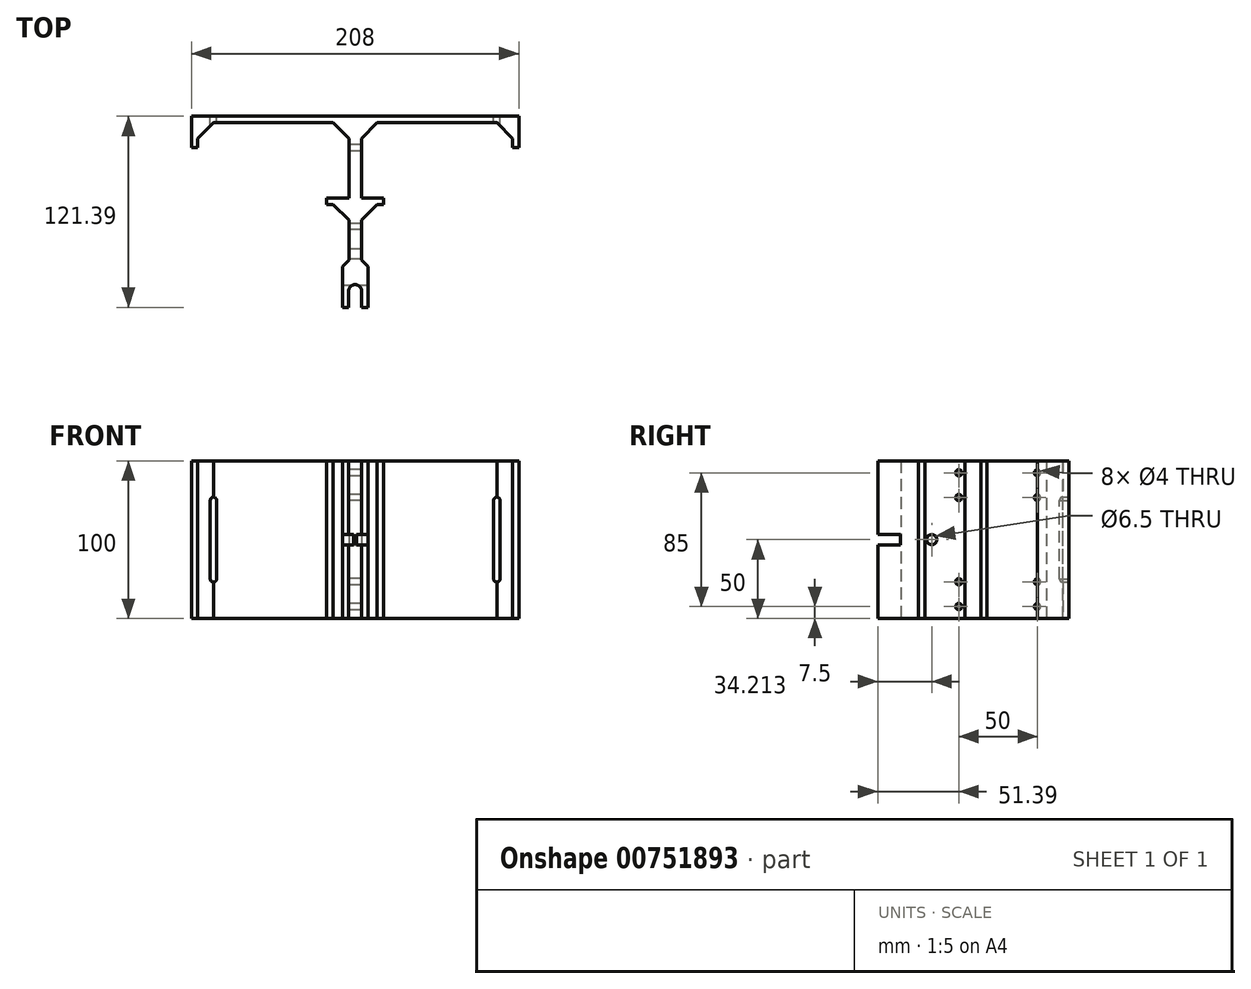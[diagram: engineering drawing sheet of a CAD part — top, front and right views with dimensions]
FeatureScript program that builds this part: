
annotation { "Feature Type Name" : "Feature", "Feature Type Description" : "" }
export const myFeature = defineFeature(function(context is Context, id is Id, definition is map)
    precondition{}
    {
        {
            assignVariable(context, id + "F0", {"name" : "width", "anyValue" : 100});
        }
        {
            var Q0;
            Q0=qCreatedBy(makeId("Top.planeOp"),FACE);
            var sketch = newSketch(context, id + "F1", { "sketchPlane" : qUnion([Q0])});
            skLineSegment(sketch, "E0", {"start": v(-8.12, -10.4) * mm, "end": v(-8.12, 9.6) * mm});
            skLineSegment(sketch, "E1", {"start": v(-8.12, 9.6) * mm, "end": v(-4, 9.6) * mm});
            skLineSegment(sketch, "E2", {"start": v(-4, 9.6) * mm, "end": v(-4, 55) * mm});
            skLineSegment(sketch, "E3", {"start": v(-4, 107) * mm, "end": v(-100, 107) * mm});
            skLineSegment(sketch, "E4", {"start": v(-100, 107) * mm, "end": v(-100, 91) * mm});
            skLineSegment(sketch, "E5", {"start": v(-100, 91) * mm, "end": v(-104, 91) * mm});
            skLineSegment(sketch, "E6", {"start": v(-104, 91) * mm, "end": v(-104, 111) * mm});
            skLineSegment(sketch, "E7", {"start": v(-104, 111) * mm, "end": v(0, 111) * mm});
            skCircle(sketch, "E8", {"center": v(0, 0) * mm, "radius": 4.12 * mm});
            skLineSegment(sketch, "E9.bottom", {"start": v(-4, 55) * mm, "end": v(-18, 55) * mm});
            skLineSegment(sketch, "E9.top", {"start": v(-4, 59) * mm, "end": v(-18, 59) * mm});
            skLineSegment(sketch, "E9.right", {"start": v(-18, 55) * mm, "end": v(-18, 59) * mm});
            skLineSegment(sketch, "E10.bottom", {"start": v(-32, 87) * mm, "end": v(-4, 87) * mm, "construction": true});
            skLineSegment(sketch, "E10.top", {"start": v(-32, 59) * mm, "end": v(-4, 59) * mm, "construction": true});
            skLineSegment(sketch, "E10.left", {"start": v(-32, 87) * mm, "end": v(-32, 59) * mm, "construction": true});
            skLineSegment(sketch, "E10.right", {"start": v(-4, 87) * mm, "end": v(-4, 59) * mm, "construction": true});
            skPoint(sketch, "E11", {"position": v(-18, 73) * mm});
            skLineSegment(sketch, "E12", {"start": v(-4.12, 0) * mm, "end": v(-4.12, -10.4) * mm});
            skLineSegment(sketch, "E13", {"start": v(-4.12, -10.4) * mm, "end": v(-8.12, -10.4) * mm});
            skLineSegment(sketch, "E14.MirrorCS", {"start": v(18, 55) * mm, "end": v(18, 59) * mm});
            skLineSegment(sketch, "E15.MirrorCS", {"start": v(100, 91) * mm, "end": v(104, 91) * mm});
            skLineSegment(sketch, "E16.MirrorCS", {"start": v(4, 59) * mm, "end": v(18, 59) * mm});
            skPoint(sketch, "E17.MirrorP", {"position": v(18, 73) * mm});
            skLineSegment(sketch, "E18.MirrorCS", {"start": v(4.12, 0) * mm, "end": v(4.12, -10.4) * mm});
            skLineSegment(sketch, "E19.MirrorCS", {"start": v(32, 87) * mm, "end": v(4, 87) * mm, "construction": true});
            skLineSegment(sketch, "E20.MirrorCS", {"start": v(32, 59) * mm, "end": v(4, 59) * mm, "construction": true});
            skLineSegment(sketch, "E21.MirrorCS", {"start": v(4.12, -10.4) * mm, "end": v(8.12, -10.4) * mm});
            skLineSegment(sketch, "E22.MirrorCS", {"start": v(32, 87) * mm, "end": v(32, 59) * mm, "construction": true});
            skLineSegment(sketch, "E23.MirrorCS", {"start": v(4, 87) * mm, "end": v(4, 59) * mm, "construction": true});
            skLineSegment(sketch, "E24.MirrorCS", {"start": v(8.12, 9.6) * mm, "end": v(4, 9.6) * mm});
            skLineSegment(sketch, "E25.MirrorCS", {"start": v(4, 107) * mm, "end": v(100, 107) * mm});
            skLineSegment(sketch, "E26.MirrorCS", {"start": v(8.13, -10.4) * mm, "end": v(8.12, 9.6) * mm});
            skLineSegment(sketch, "E27.MirrorCS", {"start": v(4, 9.6) * mm, "end": v(4, 55) * mm});
            skLineSegment(sketch, "E28.MirrorCS", {"start": v(4, 55) * mm, "end": v(18, 55) * mm});
            skLineSegment(sketch, "E29.MirrorCS", {"start": v(104, 111) * mm, "end": v(0, 111) * mm});
            skLineSegment(sketch, "E30.MirrorCS", {"start": v(100, 107) * mm, "end": v(100, 91) * mm});
            skLineSegment(sketch, "E31.MirrorCS", {"start": v(104, 91) * mm, "end": v(104, 111) * mm});
            skLineSegment(sketch, "E32.trimOffspring", {"start": v(-4, 59) * mm, "end": v(-4, 107) * mm});
            skLineSegment(sketch, "E33.trimOffspring", {"start": v(4, 59) * mm, "end": v(4, 107) * mm});
            skPoint(sketch, "E34", {"position": v(-90, 111) * mm});
            skPoint(sketch, "E35.MirrorP", {"position": v(90, 111) * mm});
            skSolve(sketch);
        }
        {
            var Q0;
            Q0=makeQuery(id+"F1.imprint","IMPRINT",FACE,{"disambiguationData":[TD([[makeQuery(id+"F1.imprint","IMPRINT",EDGE,{"derivedFrom":sQuery(id+"F1.wireOp",EDGE,"E0")}),-1.0]])]});
            extrude(context, id + "F2", {"entities" : qUnion([Q0]), "endBound" : BoundingType.SYMMETRIC, "depth" : (getVariable(context, 'width')) * mm, "offsetDistance" : 25 * mm});
        }
        {
            var Q0;
            Q0=makeQuery(id+"F2.opExtrude","SWEPT_EDGE",EDGE,{"disambiguationData":[OSD([sQuery(id+"F1.wireOp",EDGE,"E27.MirrorCS"),sQuery(id+"F1.wireOp",EDGE,"E28.MirrorCS")])]});
            var Q1;
            Q1=makeQuery(id+"F2.opExtrude","SWEPT_EDGE",EDGE,{"disambiguationData":[OSD([sQuery(id+"F1.wireOp",EDGE,"E2"),sQuery(id+"F1.wireOp",EDGE,"E9.bottom")])]});
            var Q2;
            Q2=makeQuery(id+"F2.opExtrude","SWEPT_EDGE",EDGE,{"disambiguationData":[OSD([sQuery(id+"F1.wireOp",EDGE,"E25.MirrorCS"),sQuery(id+"F1.wireOp",EDGE,"E33.trimOffspring")])]});
            var Q3;
            Q3=makeQuery(id+"F2.opExtrude","SWEPT_EDGE",EDGE,{"disambiguationData":[OSD([sQuery(id+"F1.wireOp",EDGE,"E3"),sQuery(id+"F1.wireOp",EDGE,"E32.trimOffspring")])]});
            var Q4;
            Q4=makeQuery(id+"F2.opExtrude","SWEPT_EDGE",EDGE,{"disambiguationData":[OSD([sQuery(id+"F1.wireOp",EDGE,"E25.MirrorCS"),sQuery(id+"F1.wireOp",EDGE,"E30.MirrorCS")])]});
            var Q5;
            Q5=makeQuery(id+"F2.opExtrude","SWEPT_EDGE",EDGE,{"disambiguationData":[OSD([sQuery(id+"F1.wireOp",EDGE,"E3"),sQuery(id+"F1.wireOp",EDGE,"E4")])]});
            var Q6;
            Q6=makeQuery(id+"F2.opExtrude","SWEPT_EDGE",EDGE,{"disambiguationData":[OSD([sQuery(id+"F1.wireOp",EDGE,"E24.MirrorCS"),sQuery(id+"F1.wireOp",EDGE,"E27.MirrorCS")])]});
            var Q7;
            Q7=makeQuery(id+"F2.opExtrude","SWEPT_EDGE",EDGE,{"disambiguationData":[OSD([sQuery(id+"F1.wireOp",EDGE,"E1"),sQuery(id+"F1.wireOp",EDGE,"E2")])]});
            chamfer(context, id + "F3", {"entities" : qUnion([Q0, Q1, Q2, Q3, Q4, Q5, Q6, Q7]), "width" : 10 * mm, "tangentPropagation" : true});
        }
        {
            var Q0;
            Q0=makeQuery(id+"F2.opExtrude","SWEPT_FACE",FACE,{"disambiguationData":[OSD([sQuery(id+"F1.wireOp",EDGE,"E7"),sQuery(id+"F1.wireOp",EDGE,"E29.MirrorCS")])]});
            var sketch = newSketch(context, id + "F4", { "sketchPlane" : qUnion([Q0])});
            skPoint(sketch, "E36.0", {"position": v(90, 0) * mm});
            skPoint(sketch, "E37.0", {"position": v(-90, 0) * mm});
            skSolve(sketch);
        }
        {
            var Q0;
            Q0=makeQuery(id+"F2.opExtrude","SWEPT_FACE",FACE,{"disambiguationData":[OSD([sQuery(id+"F1.wireOp",EDGE,"E32.trimOffspring")])]});
            var sketch = newSketch(context, id + "F5", { "sketchPlane" : qUnion([Q0])});
            skLineSegment(sketch, "E38.bottom", {"start": v(-59, -50) * mm, "end": v(-87, -50) * mm, "construction": true});
            skLineSegment(sketch, "E38.top", {"start": v(-59, -19.25) * mm, "end": v(-87, -19.25) * mm, "construction": true});
            skLineSegment(sketch, "E38.left", {"start": v(-59, -50) * mm, "end": v(-59, -19.25) * mm, "construction": true});
            skLineSegment(sketch, "E38.right", {"start": v(-87, -50) * mm, "end": v(-87, -19.25) * mm, "construction": true});
            skLineSegment(sketch, "E39.bottom", {"start": v(-59, 50) * mm, "end": v(-87, 50) * mm, "construction": true});
            skLineSegment(sketch, "E39.top", {"start": v(-59, 19.25) * mm, "end": v(-87, 19.25) * mm, "construction": true});
            skLineSegment(sketch, "E39.left", {"start": v(-59, 50) * mm, "end": v(-59, 19.25) * mm, "construction": true});
            skLineSegment(sketch, "E39.right", {"start": v(-87, 50) * mm, "end": v(-87, 19.25) * mm, "construction": true});
            skCircle(sketch, "E40", {"center": v(-91, -26.75) * mm, "radius": 2 * mm});
            skCircle(sketch, "E41", {"center": v(-91, -42.5) * mm, "radius": 2 * mm});
            skCircle(sketch, "E42", {"center": v(-41, -26.75) * mm, "radius": 2 * mm});
            skCircle(sketch, "E43", {"center": v(-41, -42.5) * mm, "radius": 2 * mm});
            skCircle(sketch, "E44.MirrorC", {"center": v(-41, 26.75) * mm, "radius": 2 * mm});
            skCircle(sketch, "E45.MirrorC", {"center": v(-41, 42.5) * mm, "radius": 2 * mm});
            skCircle(sketch, "E46.MirrorC", {"center": v(-91, 42.5) * mm, "radius": 2 * mm});
            skCircle(sketch, "E47.MirrorC", {"center": v(-91, 26.75) * mm, "radius": 2 * mm});
            skSolve(sketch);
        }
        {
            var Q0;
            Q0 = qSketchRegion(id + "F5", true);
            extrude(context, id + "F6", {"entities" : qUnion([Q0]), "operationType" : NewBodyOperationType.REMOVE, "endBound" : BoundingType.UP_TO_NEXT, "oppositeDirection" : true, "depth" : 25 * mm, "offsetDistance" : 25 * mm});
        }
        {
            var Q0;
            {var subQ0=sQuery(id+"F1.wireOp",EDGE,"E7");Q0=makeQuery(id+"F4.imprint","IMPRINT",FACE,{"disambiguationData":[TD([[makeQuery(id+"F4.imprint","IMPRINT",EDGE,{"derivedFrom":makeQuery(id+"F2.opExtrude","SWEPT_EDGE",EDGE,{"disambiguationData":[OSD([sQuery(id+"F1.wireOp",EDGE,"E6"),subQ0])]})}),-1.0]])]});}
            var sketch = newSketch(context, id + "F7", { "sketchPlane" : qUnion([Q0])});
            skPoint(sketch, "E48.0", {"position": v(-90, 0) * mm});
            skPoint(sketch, "E49.0", {"position": v(90, 0) * mm});
            skArc(sketch, "E50", {"start": v(-92, -24.92) * mm, "mid": v(-89.98, -27) * mm, "end": v(-88, -24.88) * mm});
            skLineSegment(sketch, "E51", {"start": v(-92, -24.92) * mm, "end": v(-92, 0) * mm});
            skLineSegment(sketch, "E52", {"start": v(-88, -24.88) * mm, "end": v(-88, 0) * mm});
            skArc(sketch, "E53.MirrorC", {"start": v(-92, 24.92) * mm, "mid": v(-89.98, 27) * mm, "end": v(-88, 24.88) * mm});
            skLineSegment(sketch, "E54.MirrorCS", {"start": v(-88, 24.88) * mm, "end": v(-88, 0) * mm});
            skLineSegment(sketch, "E55.MirrorCS", {"start": v(-92, 24.92) * mm, "end": v(-92, 0) * mm});
            skLineSegment(sketch, "E56.MirrorCS", {"start": v(88, -24.88) * mm, "end": v(88, 0) * mm});
            skArc(sketch, "E57.MirrorCS", {"start": v(92, -24.92) * mm, "mid": v(89.98, -27) * mm, "end": v(88, -24.88) * mm});
            skArc(sketch, "E58.MirrorCS", {"start": v(92, 24.92) * mm, "mid": v(89.98, 27) * mm, "end": v(88, 24.88) * mm});
            skLineSegment(sketch, "E59.MirrorCS", {"start": v(92, -24.92) * mm, "end": v(92, 0) * mm});
            skLineSegment(sketch, "E60.MirrorCS", {"start": v(92, 24.92) * mm, "end": v(92, 0) * mm});
            skLineSegment(sketch, "E61.MirrorCS", {"start": v(88, 24.88) * mm, "end": v(88, 0) * mm});
            skSolve(sketch);
        }
        {
            var Q0;
            Q0 = qSketchRegion(id + "F7", true);
            extrude(context, id + "F8", {"entities" : qUnion([Q0]), "operationType" : NewBodyOperationType.REMOVE, "endBound" : BoundingType.UP_TO_NEXT, "oppositeDirection" : true, "depth" : 25 * mm, "offsetDistance" : 25 * mm});
        }
        {
            var Q0;
            Q0=makeQuery(id+"F2.opExtrude","SWEPT_FACE",FACE,{"disambiguationData":[OSD([sQuery(id+"F1.wireOp",EDGE,"E26.MirrorCS")])]});
            var sketch = newSketch(context, id + "F9", { "sketchPlane" : qUnion([Q0])});
            skLineSegment(sketch, "E62.top", {"start": v(-10.4, 3.25) * mm, "end": v(4, 3.25) * mm});
            skLineSegment(sketch, "E62.left", {"start": v(-10.4, 0) * mm, "end": v(-10.4, 3.25) * mm});
            skLineSegment(sketch, "E62.right", {"start": v(4, 0) * mm, "end": v(4, 3.25) * mm});
            skLineSegment(sketch, "E63.MirrorCS", {"start": v(4, 0) * mm, "end": v(4, -3.25) * mm});
            skLineSegment(sketch, "E64.MirrorCS", {"start": v(-10.4, 0) * mm, "end": v(-10.4, -3.25) * mm});
            skLineSegment(sketch, "E65.MirrorCS", {"start": v(-10.4, -3.25) * mm, "end": v(4, -3.25) * mm});
            skCircle(sketch, "E66", {"center": v(23.82, 0) * mm, "radius": 3.25 * mm});
            skSolve(sketch);
        }
        {
            var Q0;
            Q0=makeQuery(id+"F9.imprint","IMPRINT",FACE,{"disambiguationData":[TD([[makeQuery(id+"F9.imprint","IMPRINT",EDGE,{"derivedFrom":sQuery(id+"F9.wireOp",EDGE,"E62.top")}),-1.0]])]});
            var Q1;
            Q1=makeQuery(id+"F9.imprint","IMPRINT",FACE,{"disambiguationData":[TD([[makeQuery(id+"F9.imprint","IMPRINT",EDGE,{"derivedFrom":sQuery(id+"F9.wireOp",EDGE,"E66")}),1.0]])]});
            extrude(context, id + "F10", {"entities" : qUnion([Q0, Q1]), "operationType" : NewBodyOperationType.REMOVE, "oppositeDirection" : true, "depth" : 25 * mm, "offsetDistance" : 25 * mm});
        }
    });
